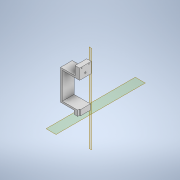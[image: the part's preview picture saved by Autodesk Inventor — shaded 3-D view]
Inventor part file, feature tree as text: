
AUTODESK INVENTOR PART (.ipt)
format: ipt  version: 2020 (Build 240168000, 168)  size: 208,896 bytes
history: native  units: mm
features: reference x19, other x11, sketch x7, projected_geometry x6, extrude x5, hole x2
ambient origin geometry x8: Origin, YZ Plane, XZ Plane, XY Plane, X Axis, Y Axis, Z Axis, Center Point
bodies: Body1 (feature_tree)
feature tree (50):
  other  "솔리드1"
  other  "작업 평면1"
  extrude  "돌출1"  Depth=67.0mm TaperAngle=0.0deg
  other  "작업 평면2"
  extrude  "돌출2"  Depth=67.0mm TaperAngle=0.0deg
  hole  "구멍1"  [1 undecoded]
  hole  "구멍2"  [1 undecoded]
  extrude  "돌출4"  Depth=10.0mm
  extrude  "돌출5"  Depth=150.2mm
  extrude  "돌출6"  Depth=1.0mm TaperAngle=0.0deg
  sketch  "스케치1"
  reference  "참조1"
  reference  "참조2"
  reference  "참조3"
  reference  "참조4"
  reference  "참조5"
  reference  "참조6"
  reference  "참조7"
  reference  "참조8"
  reference  "참조9"
  reference  "참조10"
  reference  "참조11"
  reference  "참조12"
  reference  "참조13"
  reference  "참조14"
  sketch  "스케치2"
  reference  "참조15"
  projected_geometry  "투영된 루프1"
  reference  "참조16"
  sketch  "스케치6"
  reference  "참조23"
  reference  "참조24"
  projected_geometry  "투영된 루프3"
  projected_geometry  "투영된 루프4"
  sketch  "스케치9"
  reference  "참조25"
  sketch  "스케치10"
  projected_geometry  "투영된 루프5"
  sketch  "스케치11"
  projected_geometry  "투영된 루프6"
  sketch  "스케치13"
  projected_geometry  "투영된 루프8"
  parser-record x1  (decoder bookkeeping rows leaked as tree rows — omitted from the tree; the rows remain in map.json)
  other  "v6.iam"
  other  "AL_profile_final:1"
  other  "bumper_final_6:2"
  other  "Axel_arch_final_v4:2"
  other  "Axel_crossbar_final_v2:2"
  other  "cross_AL_profile:2"
  other  "STM_Rear:1"
note: 2 required parameter values undecoded (feature->parameter linkage not recoverable at this tier; creation-order binding heuristic only, values carry confidence <= 0.55)
note: 1 file-system path scrubbed to <path> (originals preserved in map.json)
